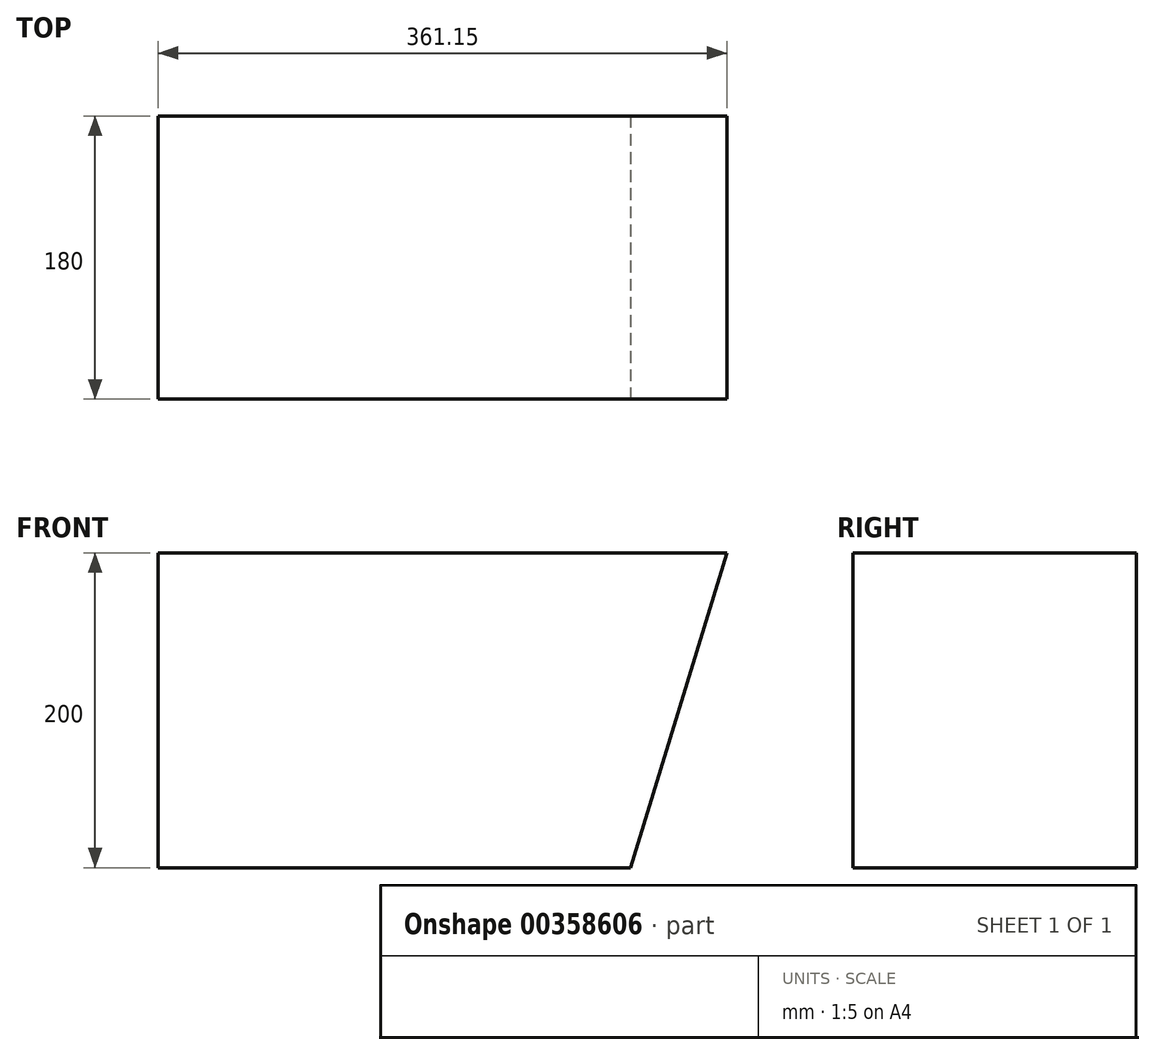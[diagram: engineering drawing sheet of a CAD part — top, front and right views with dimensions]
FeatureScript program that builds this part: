
annotation { "Feature Type Name" : "Feature", "Feature Type Description" : "" }
export const myFeature = defineFeature(function(context is Context, id is Id, definition is map)
    precondition{}
    {
        {
            var Q0;
            Q0=qCreatedBy(makeId("Front.planeOp"),FACE);
            var sketch = newSketch(context, id + "F0", { "sketchPlane" : qUnion([Q0])});
            skLineSegment(sketch, "E0.bottom", {"start": v(150, -100) * mm, "end": v(-150, -100) * mm});
            skLineSegment(sketch, "E0.top", {"start": v(150, 100) * mm, "end": v(-150, 100) * mm});
            skLineSegment(sketch, "E0.left", {"start": v(150, -100) * mm, "end": v(150, 100) * mm});
            skLineSegment(sketch, "E0.right", {"start": v(-150, -100) * mm, "end": v(-150, 100) * mm});
            skPoint(sketch, "E0.middle", {"position": v(0, 0) * mm});
            skSolve(sketch);
        }
        {
            var Q0;
            Q0 = qSketchRegion(id + "F0", true);
            extrude(context, id + "F1", {"entities" : qUnion([Q0]), "oppositeDirection" : true, "depth" : 180 * mm});
        }
        {
            var Q0;
            Q0=makeQuery(id+"F1.opExtrude","CAP_FACE",FACE,{"disambiguationData":[OSD([sQuery(id+"F0.wireOp",EDGE,"E0.bottom"),sQuery(id+"F0.wireOp",EDGE,"E0.top"),sQuery(id+"F0.wireOp",EDGE,"E0.left"),sQuery(id+"F0.wireOp",EDGE,"E0.right")])],"isStart":true});
            var sketch = newSketch(context, id + "F2", { "sketchPlane" : qUnion([Q0])});
            skLineSegment(sketch, "E1", {"start": v(150, -100) * mm, "end": v(211.15, 100) * mm});
            skLineSegment(sketch, "E2", {"start": v(211.15, 100) * mm, "end": v(150, 100) * mm});
            skSolve(sketch);
        }
        {
            var Q0;
            Q0=makeQuery(id+"F2.imprint","IMPRINT",FACE,{"disambiguationData":[TD([[makeQuery(id+"F2.imprint","IMPRINT",EDGE,{"derivedFrom":sQuery(id+"F2.wireOp",EDGE,"E1")}),1.0]])]});
            extrude(context, id + "F3", {"entities" : qUnion([Q0]), "operationType" : NewBodyOperationType.ADD, "oppositeDirection" : true, "depth" : 180 * mm});
        }
    });
